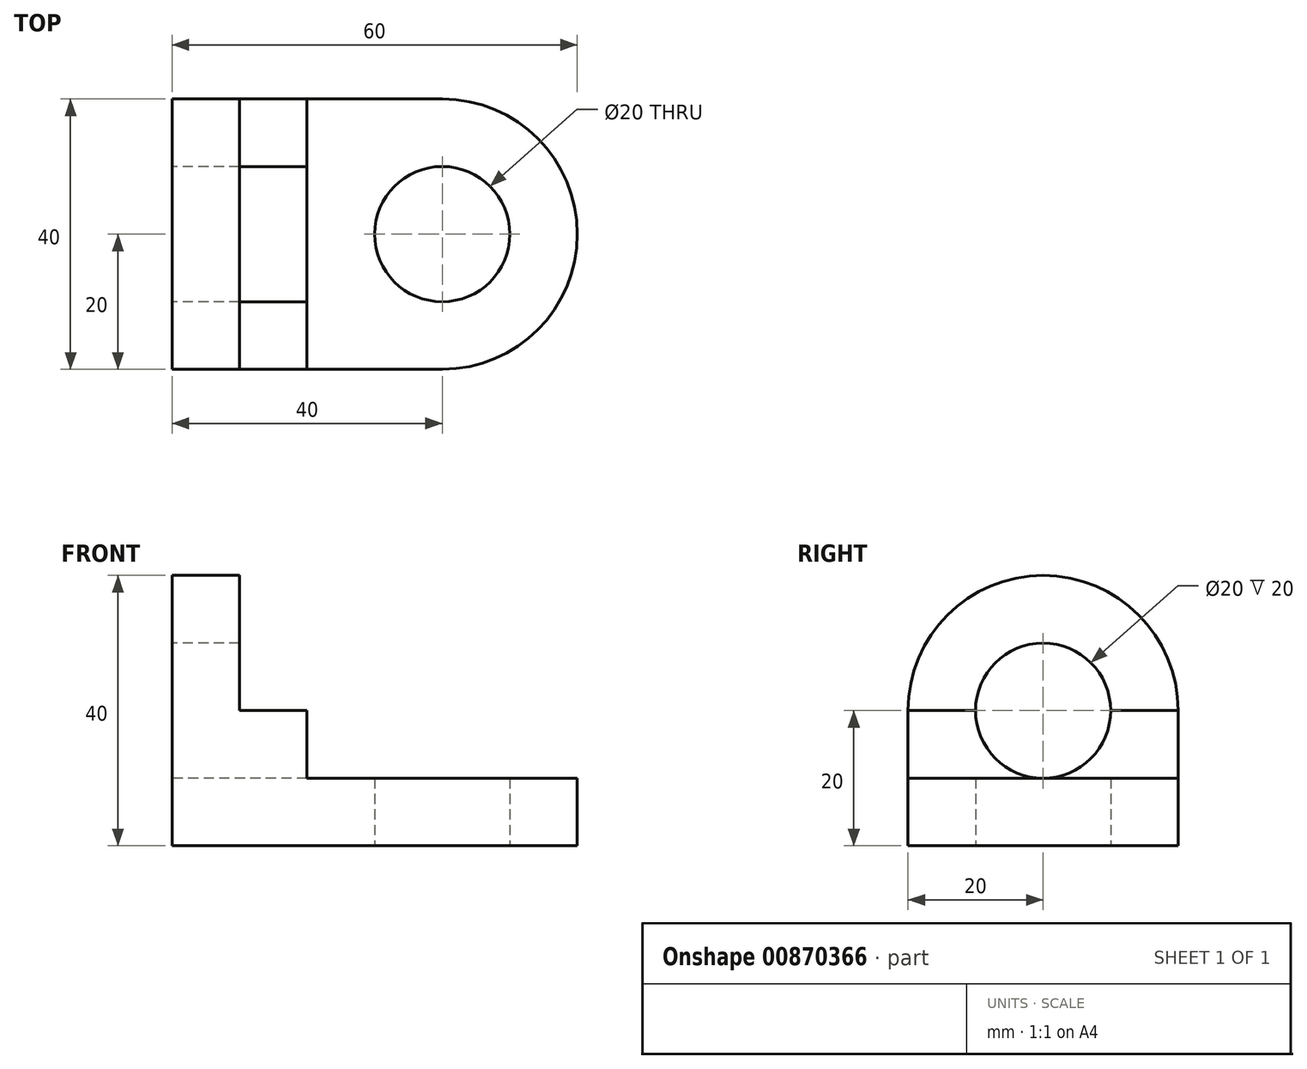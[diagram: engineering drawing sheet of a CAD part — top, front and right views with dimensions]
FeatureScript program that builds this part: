
annotation { "Feature Type Name" : "Feature", "Feature Type Description" : "" }
export const myFeature = defineFeature(function(context is Context, id is Id, definition is map)
    precondition{}
    {
        {
            var Q0;
            Q0=qCreatedBy(makeId("Right.planeOp"),FACE);
            var sketch = newSketch(context, id + "F0", { "sketchPlane" : qUnion([Q0])});
            skLineSegment(sketch, "E0.bottom", {"start": v(-20, 0) * mm, "end": v(20, 0) * mm});
            skArc(sketch, "E1", {"start": v(20, 20) * mm, "mid": v(0, 40) * mm, "end": v(-20, 20) * mm});
            skLineSegment(sketch, "E2", {"start": v(-20, 0) * mm, "end": v(-20, 20) * mm});
            skLineSegment(sketch, "E3", {"start": v(20, 0) * mm, "end": v(20, 20) * mm});
            skLineSegment(sketch, "E4.trimOffspring", {"start": v(0, 0) * mm, "end": v(0, 0) * mm});
            skCircle(sketch, "E5", {"center": v(0, 20) * mm, "radius": 10 * mm});
            skSolve(sketch);
        }
        {
            var Q0;
            Q0 = qSketchRegion(id + "F0", true);
            extrude(context, id + "F1", {"entities" : qUnion([Q0]), "depth" : 20 * mm, "offsetDistance" : 25 * mm});
        }
        {
            var Q0;
            Q0=makeQuery(id+"F1.opExtrude","CAP_FACE",FACE,{"disambiguationData":[OSD([sQuery(id+"F0.wireOp",EDGE,"E0.bottom"),sQuery(id+"F0.wireOp",EDGE,"E1"),sQuery(id+"F0.wireOp",EDGE,"E2"),sQuery(id+"F0.wireOp",EDGE,"E3"),sQuery(id+"F0.wireOp",EDGE,"E5")])],"isStart":false});
            var sketch = newSketch(context, id + "F2", { "sketchPlane" : qUnion([Q0])});
            skArc(sketch, "E6", {"start": v(10, 20) * mm, "mid": v(0, 30) * mm, "end": v(-10, 20) * mm});
            skArc(sketch, "E7", {"start": v(20, 20) * mm, "mid": v(0, 40) * mm, "end": v(-20, 20) * mm});
            skLineSegment(sketch, "E8", {"start": v(-20, 20) * mm, "end": v(20, 20) * mm});
            skSolve(sketch);
        }
        {
            var Q0;
            Q0 = qSketchRegion(id + "F2", true);
            extrude(context, id + "F3", {"entities" : qUnion([Q0]), "operationType" : NewBodyOperationType.REMOVE, "oppositeDirection" : true, "depth" : 10 * mm, "offsetDistance" : 25 * mm});
        }
        {
            var Q0;
            Q0=qCreatedBy(makeId("Top.planeOp"),FACE);
            var sketch = newSketch(context, id + "F4", { "sketchPlane" : qUnion([Q0])});
            skArc(sketch, "E9", {"start": v(40, -20) * mm, "mid": v(60, 0) * mm, "end": v(40, 20) * mm});
            skCircle(sketch, "E10", {"center": v(40, 0) * mm, "radius": 10 * mm});
            skLineSegment(sketch, "E11", {"start": v(0, -20) * mm, "end": v(40, -20) * mm});
            skLineSegment(sketch, "E12", {"start": v(0, 20) * mm, "end": v(40, 20) * mm});
            skLineSegment(sketch, "E13", {"start": v(0, 20) * mm, "end": v(0, -20) * mm});
            skSolve(sketch);
        }
        {
            var Q0;
            Q0 = qSketchRegion(id + "F4", true);
            extrude(context, id + "F5", {"entities" : qUnion([Q0]), "operationType" : NewBodyOperationType.ADD, "depth" : 10 * mm, "offsetDistance" : 25 * mm});
        }
    });
